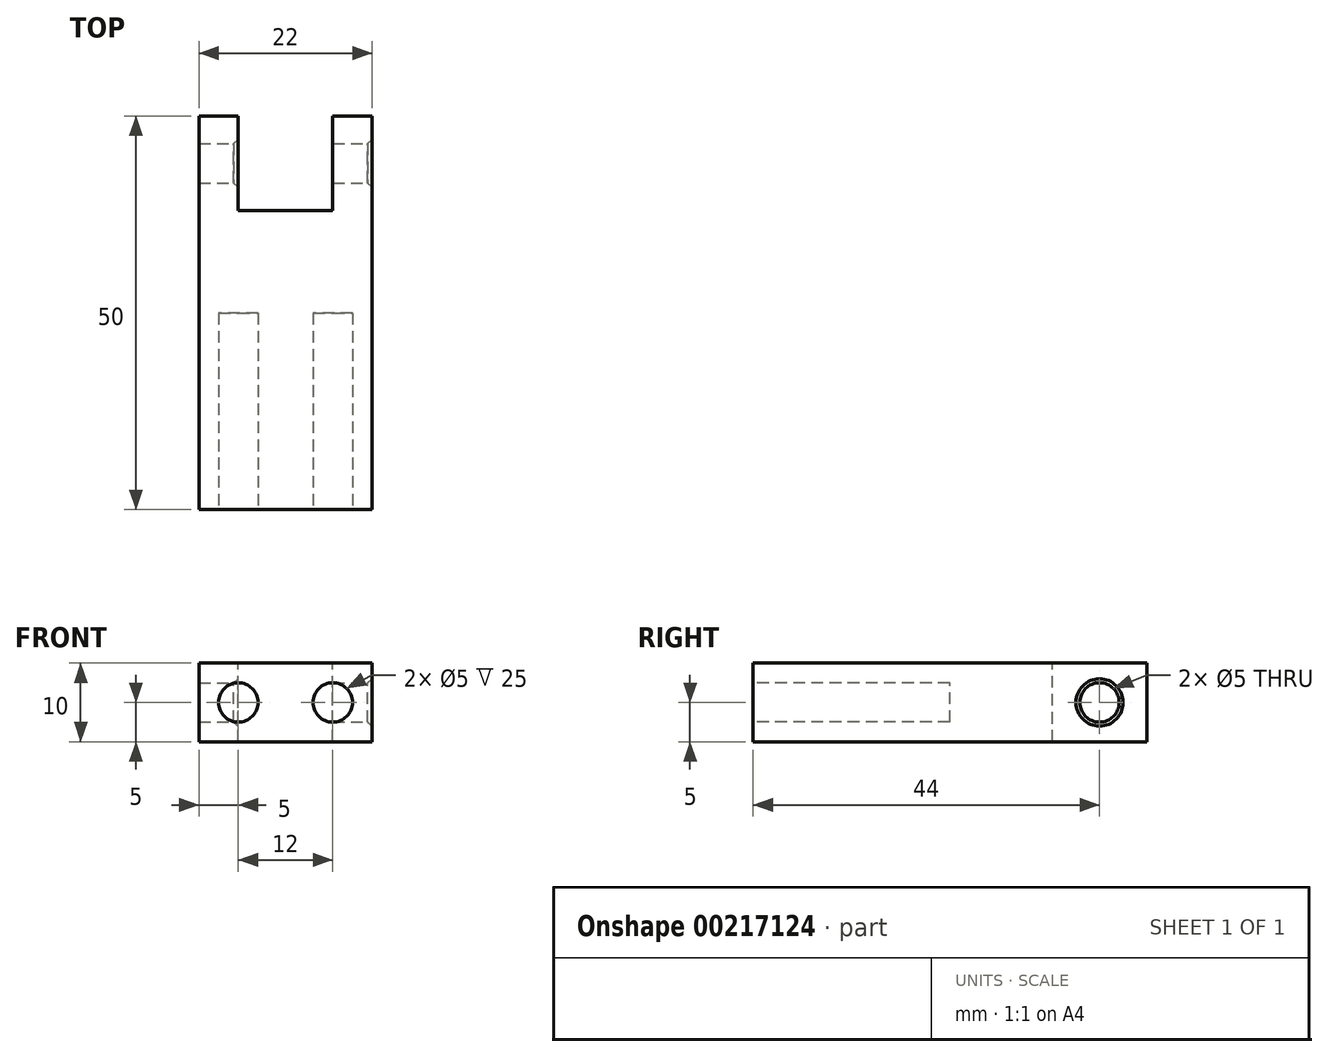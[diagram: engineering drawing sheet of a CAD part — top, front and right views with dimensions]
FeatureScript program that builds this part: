
annotation { "Feature Type Name" : "Feature", "Feature Type Description" : "" }
export const myFeature = defineFeature(function(context is Context, id is Id, definition is map)
    precondition{}
    {
        {
            var Q0;
            Q0=qCreatedBy(makeId("Front.planeOp"),FACE);
            var sketch = newSketch(context, id + "F0", { "sketchPlane" : qUnion([Q0])});
            skLineSegment(sketch, "E0.bottom", {"start": v(-11, 5) * mm, "end": v(11, 5) * mm});
            skLineSegment(sketch, "E0.top", {"start": v(-11, -5) * mm, "end": v(11, -5) * mm});
            skLineSegment(sketch, "E0.left", {"start": v(-11, 5) * mm, "end": v(-11, -5) * mm});
            skLineSegment(sketch, "E0.right", {"start": v(11, 5) * mm, "end": v(11, -5) * mm});
            skPoint(sketch, "E0.middle", {"position": v(0, 0) * mm});
            skSolve(sketch);
        }
        {
            var Q0;
            Q0=makeQuery(id+"F0.imprint","IMPRINT",FACE,{"disambiguationData":[TD([[makeQuery(id+"F0.imprint","IMPRINT",EDGE,{"derivedFrom":sQuery(id+"F0.wireOp",EDGE,"E0.bottom")}),-1.0]])]});
            var Q1;
            Q1=makeQuery(id+"F0.imprint","IMPRINT",FACE,{"disambiguationData":[TD([[makeQuery(id+"F0.imprint","IMPRINT",EDGE,{"derivedFrom":sQuery(id+"F0.wireOp",EDGE,"NJExqgRc-d67t-kyE7-JH9L-Epd90vRVJNhv")}),1.0]])]});
            var Q2;
            Q2=makeQuery(id+"F0.imprint","IMPRINT",FACE,{"disambiguationData":[TD([[makeQuery(id+"F0.imprint","IMPRINT",EDGE,{"derivedFrom":sQuery(id+"F0.wireOp",EDGE,"hwpKPeVE-sI0l-fgHY-YbTK-pLcrTsB1w373")}),1.0]])]});
            extrude(context, id + "F1", {"entities" : qUnion([Q0, Q1, Q2]), "depth" : 50 * mm});
        }
        {
            var Q0;
            Q0=makeQuery(id+"F1.opExtrude","CAP_FACE",FACE,{"disambiguationData":[OSD([sQuery(id+"F0.wireOp",EDGE,"E0.bottom"),sQuery(id+"F0.wireOp",EDGE,"E0.top"),sQuery(id+"F0.wireOp",EDGE,"E0.left"),sQuery(id+"F0.wireOp",EDGE,"E0.right")])],"isStart":false});
            var sketch = newSketch(context, id + "F2", { "sketchPlane" : qUnion([Q0])});
            skCircle(sketch, "E1", {"center": v(-6, 0) * mm, "radius": 2.5 * mm});
            skCircle(sketch, "E2", {"center": v(6, 0) * mm, "radius": 2.5 * mm});
            skSolve(sketch);
        }
        {
            var Q0;
            Q0=makeQuery(id+"F2.imprint","IMPRINT",FACE,{"disambiguationData":[TD([[makeQuery(id+"F2.imprint","IMPRINT",EDGE,{"derivedFrom":sQuery(id+"F2.wireOp",EDGE,"E2")}),1.0]])]});
            var Q1;
            Q1=makeQuery(id+"F2.imprint","IMPRINT",FACE,{"disambiguationData":[TD([[makeQuery(id+"F2.imprint","IMPRINT",EDGE,{"derivedFrom":sQuery(id+"F2.wireOp",EDGE,"E1")}),1.0]])]});
            extrude(context, id + "F3", {"entities" : qUnion([Q0, Q1]), "operationType" : NewBodyOperationType.REMOVE, "oppositeDirection" : true, "depth" : 25 * mm});
        }
        {
            var Q0;
            Q0=makeQuery(id+"F1.opExtrude","SWEPT_FACE",FACE,{"disambiguationData":[OSD([sQuery(id+"F0.wireOp",EDGE,"E0.bottom")])]});
            var sketch = newSketch(context, id + "F4", { "sketchPlane" : qUnion([Q0])});
            skLineSegment(sketch, "E3", {"start": v(-6, 0) * mm, "end": v(-6, -12) * mm});
            skLineSegment(sketch, "E4", {"start": v(-6, -12) * mm, "end": v(6, -12) * mm});
            skLineSegment(sketch, "E5", {"start": v(6, -12) * mm, "end": v(6, 0) * mm});
            skSolve(sketch);
        }
        {
            var Q0;
            {var subQ0=sQuery(id+"F4.wireOp",EDGE,"E3");Q0=makeQuery(id+"F4.imprint","IMPRINT",FACE,{"disambiguationData":[TD([[makeQuery(id+"F4.imprint","IMPRINT",EDGE,{"derivedFrom":subQ0}),1.0]])]});}
            extrude(context, id + "F5", {"entities" : qUnion([Q0]), "operationType" : NewBodyOperationType.REMOVE, "endBound" : BoundingType.THROUGH_ALL, "oppositeDirection" : true, "depth" : 25 * mm});
        }
        {
            var Q0;
            Q0=makeQuery(id+"F1.opExtrude","SWEPT_FACE",FACE,{"disambiguationData":[OSD([sQuery(id+"F0.wireOp",EDGE,"E0.right")])]});
            var sketch = newSketch(context, id + "F6", { "sketchPlane" : qUnion([Q0])});
            skPoint(sketch, "E6", {"position": v(-6, 0) * mm});
            skSolve(sketch);
        }
        {
            var Q0;
            Q0=makeQuery(id+"F5.boolean.opBoolean","COPY",FACE,{"derivedFrom":makeQuery(id+"F5.opExtrude","SWEPT_FACE",FACE,{"disambiguationData":[OSD([sQuery(id+"F4.wireOp",EDGE,"E3")])]})});
            var sketch = newSketch(context, id + "F7", { "sketchPlane" : qUnion([Q0])});
            skPoint(sketch, "E7", {"position": v(-6, 0) * mm});
            skSolve(sketch);
        }
        {
            var Q0;
            Q0=sQuery(id+"F6.wireOp",VERTEX,"E6");
            var Q1;
            Q1=sQuery(id+"F7.wireOp",VERTEX,"E7");
            var Q2;
            Q2=makeQuery(id+"F1.opExtrude","SWEPT_BODY",BODY,{"disambiguationData":[OSD([sQuery(id+"F0.wireOp",EDGE,"E0.bottom"),sQuery(id+"F0.wireOp",EDGE,"E0.top"),sQuery(id+"F0.wireOp",EDGE,"E0.left"),sQuery(id+"F0.wireOp",EDGE,"E0.right")])]});
            hole(context, id + "F8", {"style" : HoleStyle.C_SINK, "endStyle" : HoleEndStyle.THROUGH, "holeDiameter" : 5 * mm, "cSinkDiameter" : 6 * mm, "cSinkAngle" : 82 * degree, "locations" : qUnion([Q0, Q1]), "scope" : qUnion([Q2]), "isTappedThrough" : true});
        }
    });
